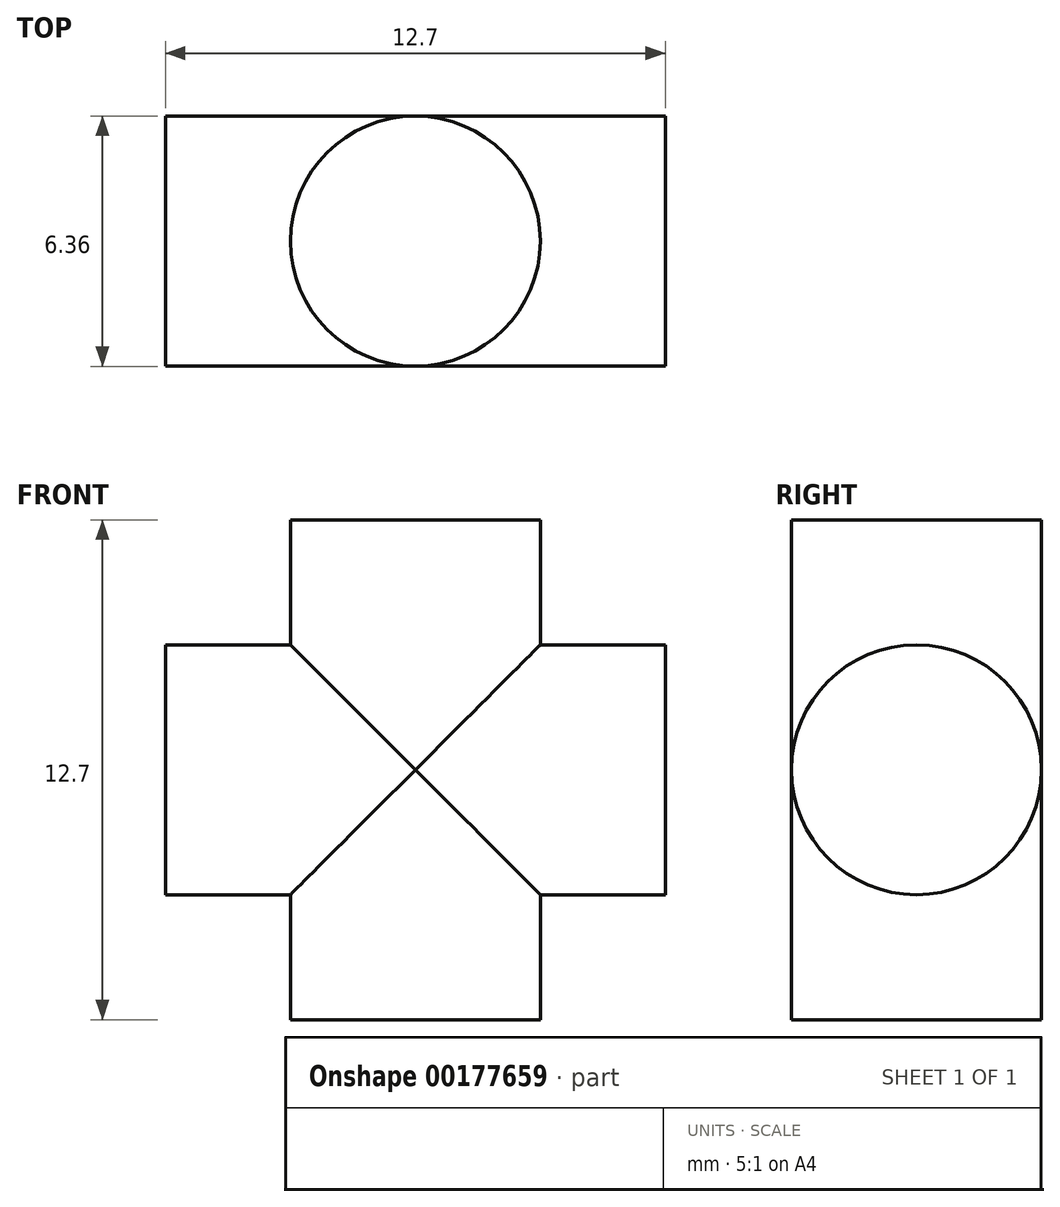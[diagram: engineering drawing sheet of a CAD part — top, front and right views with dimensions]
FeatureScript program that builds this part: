
annotation { "Feature Type Name" : "Feature", "Feature Type Description" : "" }
export const myFeature = defineFeature(function(context is Context, id is Id, definition is map)
    precondition{}
    {
        {
            var Q0;
            Q0=qCreatedBy(makeId("Top.planeOp"),FACE);
            var sketch = newSketch(context, id + "F0", { "sketchPlane" : qUnion([Q0])});
            skCircle(sketch, "E0", {"center": v(0, 0) * mm, "radius": 3.18 * mm});
            skSolve(sketch);
        }
        {
            var Q0;
            Q0 = qSketchRegion(id + "F0", true);
            extrude(context, id + "F1", {"entities" : qUnion([Q0]), "endBound" : BoundingType.SYMMETRIC, "depth" : 12.7 * mm});
        }
        {
            var Q0;
            Q0=qCreatedBy(makeId("Right.planeOp"),FACE);
            var sketch = newSketch(context, id + "F2", { "sketchPlane" : qUnion([Q0])});
            skCircle(sketch, "E1", {"center": v(0, 0) * mm, "radius": 3.18 * mm});
            skSolve(sketch);
        }
        {
            var Q0;
            Q0 = qSketchRegion(id + "F2", true);
            extrude(context, id + "F3", {"entities" : qUnion([Q0]), "operationType" : NewBodyOperationType.ADD, "endBound" : BoundingType.SYMMETRIC, "depth" : 12.7 * mm});
        }
    });
